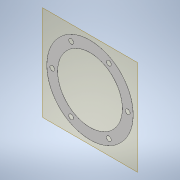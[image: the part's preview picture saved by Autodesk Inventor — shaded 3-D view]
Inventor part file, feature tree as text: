
AUTODESK INVENTOR PART (.ipt)
format: ipt  version: 2020 (Build 240168000, 168)  size: 115,712 bytes
history: native  units: mm
features: other x3, plane x1, extrude x1, sketch x1, reference x1
ambient origin geometry x8: Origin, YZ Plane, XZ Plane, XY Plane, X Axis, Y Axis, Z Axis, Center Point
bodies: 实体1 (feature_tree)
feature tree (7):
  plane  "工作平面1"
  extrude  "拉伸1"  [1 undecoded]
  sketch  "草图1"  dims[d0=0.18mm d1=0.0mm]
  reference  "参考1"
  other  "<userpath>\Desktop\ME_course_project\课设试试\shaft_try_1.iam"
  other  "shaft_try_1.iam"
  other  "轴承通盖3:1"
note: 1 required parameter value undecoded (feature->parameter linkage not recoverable at this tier; creation-order binding heuristic only, values carry confidence <= 0.55)
